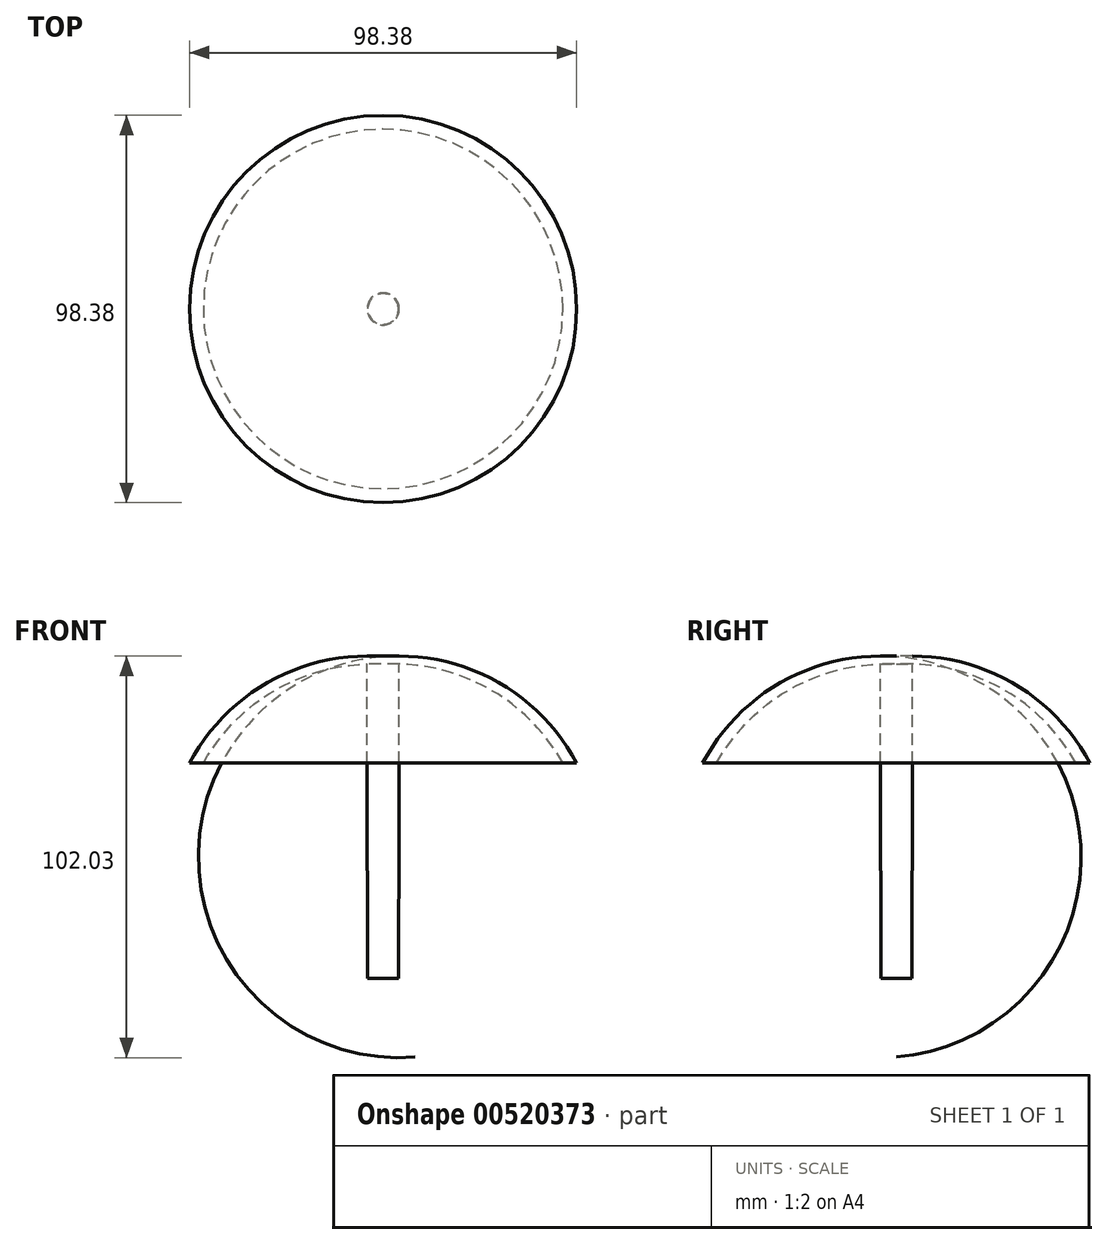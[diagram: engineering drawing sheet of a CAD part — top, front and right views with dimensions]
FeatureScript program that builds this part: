
annotation { "Feature Type Name" : "Feature", "Feature Type Description" : "" }
export const myFeature = defineFeature(function(context is Context, id is Id, definition is map)
    precondition{}
    {
        {
            var Q0;
            Q0=qCreatedBy(makeId("Front.planeOp"),FACE);
            var sketch = newSketch(context, id + "F0", { "sketchPlane" : qUnion([Q0])});
            skLineSegment(sketch, "E0", {"start": v(0, 99.53) * mm, "end": v(0, -104.32) * mm, "construction": true});
            skArc(sketch, "E1", {"start": v(49.19, 26.33) * mm, "mid": v(28.65, 47.22) * mm, "end": v(0, 53.36) * mm});
            skLineSegment(sketch, "E2", {"start": v(49.19, 26.33) * mm, "end": v(45.66, 26.33) * mm});
            skLineSegment(sketch, "E3", {"start": v(0, 26.33) * mm, "end": v(0, 53.36) * mm});
            skLineSegment(sketch, "E4", {"start": v(0, -28.37) * mm, "end": v(3.92, -28.37) * mm});
            skLineSegment(sketch, "E5", {"start": v(3.92, -28.37) * mm, "end": v(4.07, 26.33) * mm});
            skLineSegment(sketch, "E6", {"start": v(0, -28.37) * mm, "end": v(0, 26.33) * mm});
            skArc(sketch, "E7", {"start": v(45.66, 26.33) * mm, "mid": v(28.2, 44.43) * mm, "end": v(4.07, 51.5) * mm});
            skLineSegment(sketch, "E8", {"start": v(4.07, 26.33) * mm, "end": v(4.07, 51.5) * mm});
            skSolve(sketch);
        }
        {
            var Q0;
            Q0=makeQuery(id+"F0.imprint","IMPRINT",FACE,{"disambiguationData":[TD([[makeQuery(id+"F0.imprint","IMPRINT",EDGE,{"derivedFrom":sQuery(id+"F0.wireOp",EDGE,"E1")}),1.0]])]});
            var Q1;
            Q1=sQuery(id+"F0.wireOp",EDGE,"E0");
            revolve(context, id + "F1", {"entities" : qUnion([Q0]), "axis" : qUnion([Q1]), "revolveType" : RevolveType.FULL});
        }
    });
